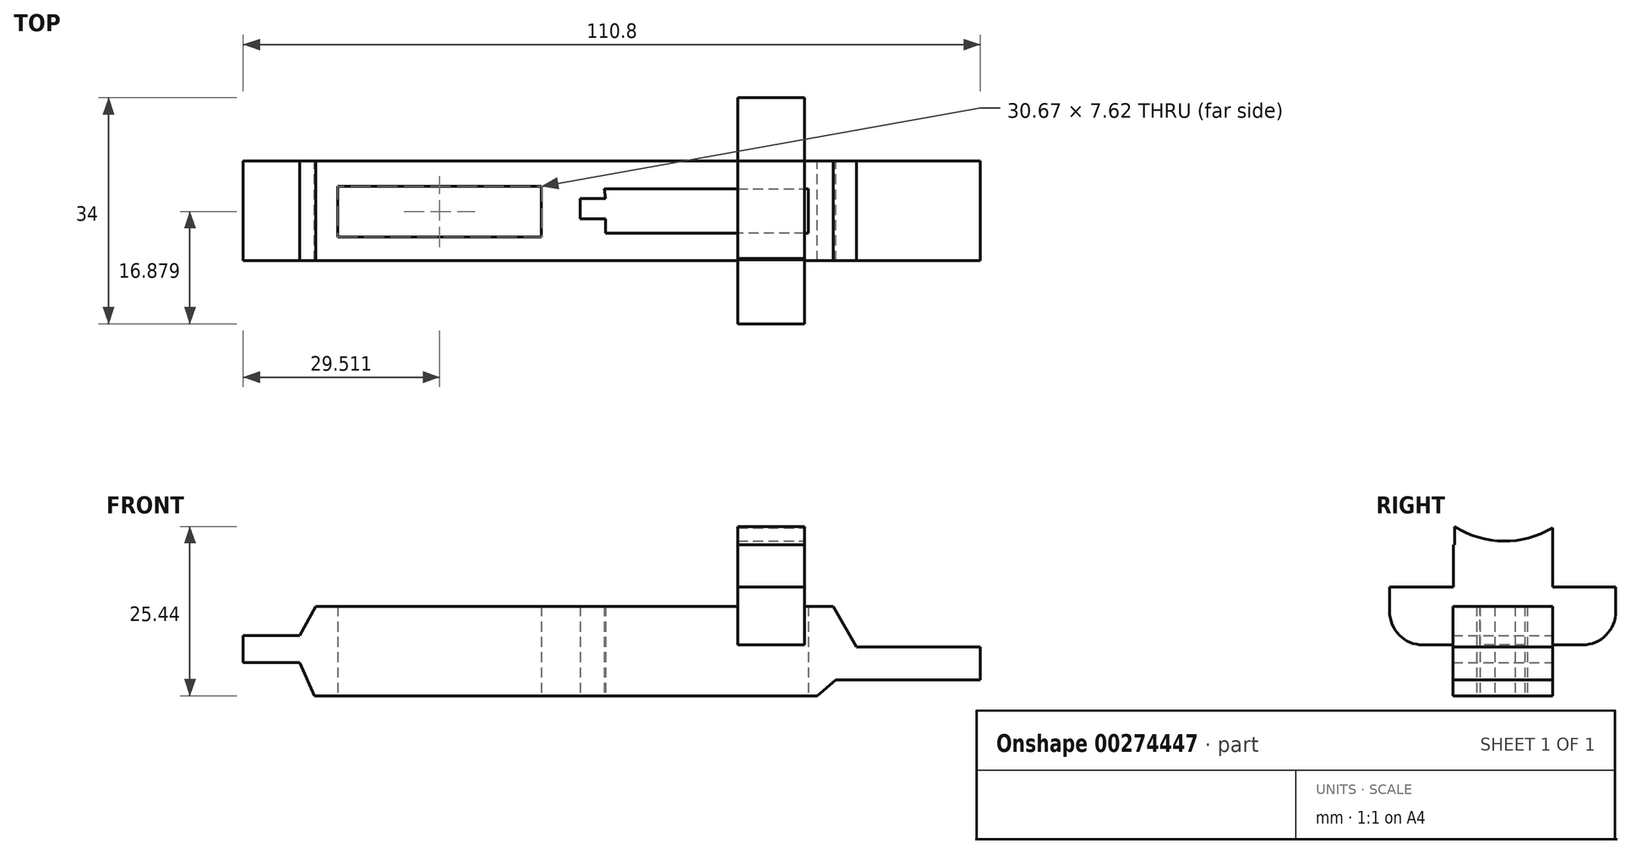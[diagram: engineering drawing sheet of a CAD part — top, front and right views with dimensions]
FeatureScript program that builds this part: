
annotation { "Feature Type Name" : "Feature", "Feature Type Description" : "" }
export const myFeature = defineFeature(function(context is Context, id is Id, definition is map)
    precondition{}
    {
        {
            var Q0;
            Q0=qCreatedBy(makeId("Front.planeOp"),FACE);
            var sketch = newSketch(context, id + "F0", { "sketchPlane" : qUnion([Q0])});
            skLineSegment(sketch, "E0", {"start": v(-48.49, 11.06) * mm, "end": v(-7.74, 11.06) * mm});
            skLineSegment(sketch, "E1", {"start": v(-7.74, 11.06) * mm, "end": v(29.31, 11.06) * mm});
            skLineSegment(sketch, "E2", {"start": v(29.31, 11.06) * mm, "end": v(32.82, 4.98) * mm});
            skLineSegment(sketch, "E3", {"start": v(32.82, 4.98) * mm, "end": v(51.44, 4.98) * mm});
            skLineSegment(sketch, "E4", {"start": v(51.44, 4.98) * mm, "end": v(51.44, 0) * mm});
            skLineSegment(sketch, "E5", {"start": v(51.44, 0) * mm, "end": v(29.68, 0) * mm});
            skLineSegment(sketch, "E6", {"start": v(29.68, 0) * mm, "end": v(26.92, -2.4) * mm});
            skLineSegment(sketch, "E7", {"start": v(26.92, -2.4) * mm, "end": v(-48.67, -2.4) * mm});
            skLineSegment(sketch, "E8", {"start": v(-48.67, -2.4) * mm, "end": v(-50.88, 2.58) * mm});
            skLineSegment(sketch, "E9", {"start": v(-50.88, 2.58) * mm, "end": v(-59.36, 2.58) * mm});
            skLineSegment(sketch, "E10", {"start": v(-59.36, 2.58) * mm, "end": v(-59.36, 6.64) * mm});
            skLineSegment(sketch, "E11", {"start": v(-59.36, 6.64) * mm, "end": v(-50.88, 6.64) * mm});
            skLineSegment(sketch, "E12", {"start": v(-50.88, 6.64) * mm, "end": v(-48.49, 11.06) * mm});
            skSolve(sketch);
        }
        {
            var Q0;
            Q0=makeQuery(id+"F0.imprint","IMPRINT",FACE,{"disambiguationData":[TD([[makeQuery(id+"F0.imprint","IMPRINT",EDGE,{"derivedFrom":sQuery(id+"F0.wireOp",EDGE,"E0")}),-1.0]])]});
            extrude(context, id + "F1", {"entities" : qUnion([Q0]), "depth" : 15 * mm});
        }
        {
            var Q0;
            Q0=qCreatedBy(makeId("Top.planeOp"),FACE);
            var sketch = newSketch(context, id + "F2", { "sketchPlane" : qUnion([Q0])});
            skLineSegment(sketch, "E13.bottom", {"start": v(-45.18, -3.81) * mm, "end": v(-14.52, -3.81) * mm});
            skLineSegment(sketch, "E13.top", {"start": v(-45.18, -11.43) * mm, "end": v(-14.52, -11.43) * mm});
            skLineSegment(sketch, "E13.left", {"start": v(-45.18, -3.81) * mm, "end": v(-45.18, -11.43) * mm});
            skLineSegment(sketch, "E13.right", {"start": v(-14.52, -3.81) * mm, "end": v(-14.52, -11.43) * mm});
            skSolve(sketch);
        }
        {
            var Q0;
            Q0 = qSketchRegion(id + "F2", true);
            extrude(context, id + "F3", {"entities" : qUnion([Q0]), "operationType" : NewBodyOperationType.REMOVE, "endBound" : BoundingType.THROUGH_ALL, "depth" : 25 * mm});
        }
        {
            var Q0;
            Q0=makeQuery(id+"F3.boolean.opBoolean","COPY",FACE,{"derivedFrom":makeQuery(id+"F3.opExtrude","CAP_FACE",FACE,{"disambiguationData":[OSD([sQuery(id+"F2.wireOp",EDGE,"E13.bottom"),sQuery(id+"F2.wireOp",EDGE,"E13.top"),sQuery(id+"F2.wireOp",EDGE,"E13.left"),sQuery(id+"F2.wireOp",EDGE,"E13.right")])],"isStart":true})});
            extrude(context, id + "F4", {"entities" : qUnion([Q0]), "operationType" : NewBodyOperationType.REMOVE, "endBound" : BoundingType.THROUGH_ALL, "oppositeDirection" : true, "depth" : 25 * mm});
        }
        {
            var Q0;
            Q0=qCreatedBy(makeId("Top.planeOp"),FACE);
            var sketch = newSketch(context, id + "F5", { "sketchPlane" : qUnion([Q0])});
            skLineSegment(sketch, "E14", {"start": v(-5.08, -4.17) * mm, "end": v(25.58, -4.17) * mm});
            skLineSegment(sketch, "E15", {"start": v(25.58, -4.17) * mm, "end": v(25.58, -10.89) * mm});
            skLineSegment(sketch, "E16", {"start": v(25.58, -10.89) * mm, "end": v(-4.9, -10.89) * mm});
            skLineSegment(sketch, "E17", {"start": v(-4.9, -10.89) * mm, "end": v(-4.9, -8.7) * mm});
            skLineSegment(sketch, "E18", {"start": v(-4.9, -8.7) * mm, "end": v(-8.7, -8.7) * mm});
            skLineSegment(sketch, "E19", {"start": v(-8.7, -8.7) * mm, "end": v(-8.7, -5.63) * mm});
            skLineSegment(sketch, "E20", {"start": v(-8.7, -5.63) * mm, "end": v(-4.9, -5.63) * mm});
            skLineSegment(sketch, "E21", {"start": v(-4.9, -5.63) * mm, "end": v(-5.08, -4.17) * mm});
            skSolve(sketch);
        }
        {
            var Q0;
            Q0 = qSketchRegion(id + "F5", true);
            extrude(context, id + "F6", {"entities" : qUnion([Q0]), "operationType" : NewBodyOperationType.REMOVE, "endBound" : BoundingType.THROUGH_ALL, "depth" : 40 * mm});
        }
        {
            var Q0;
            Q0=makeQuery(id+"F6.boolean.opBoolean","COPY",FACE,{"derivedFrom":makeQuery(id+"F6.opExtrude","CAP_FACE",FACE,{"disambiguationData":[OSD([sQuery(id+"F5.wireOp",EDGE,"E14"),sQuery(id+"F5.wireOp",EDGE,"E15"),sQuery(id+"F5.wireOp",EDGE,"E16"),sQuery(id+"F5.wireOp",EDGE,"E17"),sQuery(id+"F5.wireOp",EDGE,"E18"),sQuery(id+"F5.wireOp",EDGE,"E19"),sQuery(id+"F5.wireOp",EDGE,"E20"),sQuery(id+"F5.wireOp",EDGE,"E21")])],"isStart":true})});
            extrude(context, id + "F7", {"entities" : qUnion([Q0]), "operationType" : NewBodyOperationType.REMOVE, "endBound" : BoundingType.THROUGH_ALL, "oppositeDirection" : true, "depth" : 25 * mm});
        }
        {
            var Q0;
            Q0=qCreatedBy(makeId("Right.planeOp"),FACE);
            cPlane(context, id + "F8", {"entities" : qUnion([Q0]), "cplaneType" : CPlaneType.OFFSET, "offset" : 25 * mm, "width" : 150 * mm, "height" : 150 * mm});
        }
        {
            var Q0;
            Q0=qCreatedBy(id+"F8.planeOp",FACE);
            var sketch = newSketch(context, id + "F9", { "sketchPlane" : qUnion([Q0])});
            skLineSegment(sketch, "E22.bottom", {"start": v(-24.5, 13.97) * mm, "end": v(-24.5, 13.97) * mm});
            skLineSegment(sketch, "E22.top", {"start": v(-24.5, 5.26) * mm, "end": v(-24.5, 5.26) * mm});
            skLineSegment(sketch, "E22.left", {"start": v(-24.5, 13.97) * mm, "end": v(-24.5, 10.26) * mm});
            skLineSegment(sketch, "E22.right", {"start": v(-24.5, 13.97) * mm, "end": v(-24.5, 10.26) * mm});
            skLineSegment(sketch, "E23.bottom", {"start": v(4.5, 5.26) * mm, "end": v(-19.5, 5.26) * mm});
            skLineSegment(sketch, "E23.top", {"start": v(9.5, 13.97) * mm, "end": v(-24.5, 13.97) * mm});
            skLineSegment(sketch, "E23.left", {"start": v(9.5, 10.26) * mm, "end": v(9.5, 13.97) * mm});
            skPoint(sketch, "E24.visualSharp", {"position": v(-24.5, 5.26) * mm});
            skArc(sketch, "E24.filletArc", {"start": v(-24.5, 10.26) * mm, "mid": v(-23.03, 6.73) * mm, "end": v(-19.5, 5.26) * mm});
            skPoint(sketch, "E25.visualSharp", {"position": v(9.5, 5.26) * mm});
            skArc(sketch, "E25.filletArc", {"start": v(4.5, 5.26) * mm, "mid": v(8.04, 6.73) * mm, "end": v(9.5, 10.26) * mm});
            skLineSegment(sketch, "E26.bottom", {"start": v(-14.88, 13.97) * mm, "end": v(-14.7, 13.97) * mm});
            skLineSegment(sketch, "E26.top", {"start": v(-14.88, 20.32) * mm, "end": v(-14.7, 20.32) * mm});
            skLineSegment(sketch, "E26.left", {"start": v(-14.88, 13.97) * mm, "end": v(-14.88, 20.32) * mm});
            skLineSegment(sketch, "E26.right", {"start": v(-14.7, 13.97) * mm, "end": v(-14.7, 20.32) * mm});
            skLineSegment(sketch, "E27.bottom", {"start": v(0, 20.32) * mm, "end": v(0, 20.32) * mm});
            skLineSegment(sketch, "E27.top", {"start": v(0, 13.97) * mm, "end": v(0, 13.97) * mm});
            skLineSegment(sketch, "E27.left", {"start": v(0, 20.32) * mm, "end": v(0, 13.97) * mm});
            skLineSegment(sketch, "E27.right", {"start": v(0, 20.32) * mm, "end": v(0, 13.97) * mm});
            skLineSegment(sketch, "E28.bottom", {"start": v(0, 20.32) * mm, "end": v(-14.7, 20.32) * mm});
            skLineSegment(sketch, "E28.top", {"start": v(0, 20.32) * mm, "end": v(-14.7, 20.32) * mm});
            skLineSegment(sketch, "E28.right", {"start": v(-14.7, 20.32) * mm, "end": v(-14.7, 20.32) * mm});
            skArc(sketch, "E29", {"start": v(-14.7, 23.04) * mm, "mid": v(-7.37, 20.87) * mm, "end": v(0, 22.86) * mm});
            skLineSegment(sketch, "E30", {"start": v(-14.7, 23.04) * mm, "end": v(-14.7, 20.32) * mm});
            skLineSegment(sketch, "E31", {"start": v(0, 22.86) * mm, "end": v(0, 20.32) * mm});
            skSolve(sketch);
        }
        {
            var Q0;
            Q0 = qSketchRegion(id + "F9", true);
            extrude(context, id + "F10", {"entities" : qUnion([Q0]), "operationType" : NewBodyOperationType.ADD, "oppositeDirection" : true, "depth" : 10 * mm});
        }
    });
